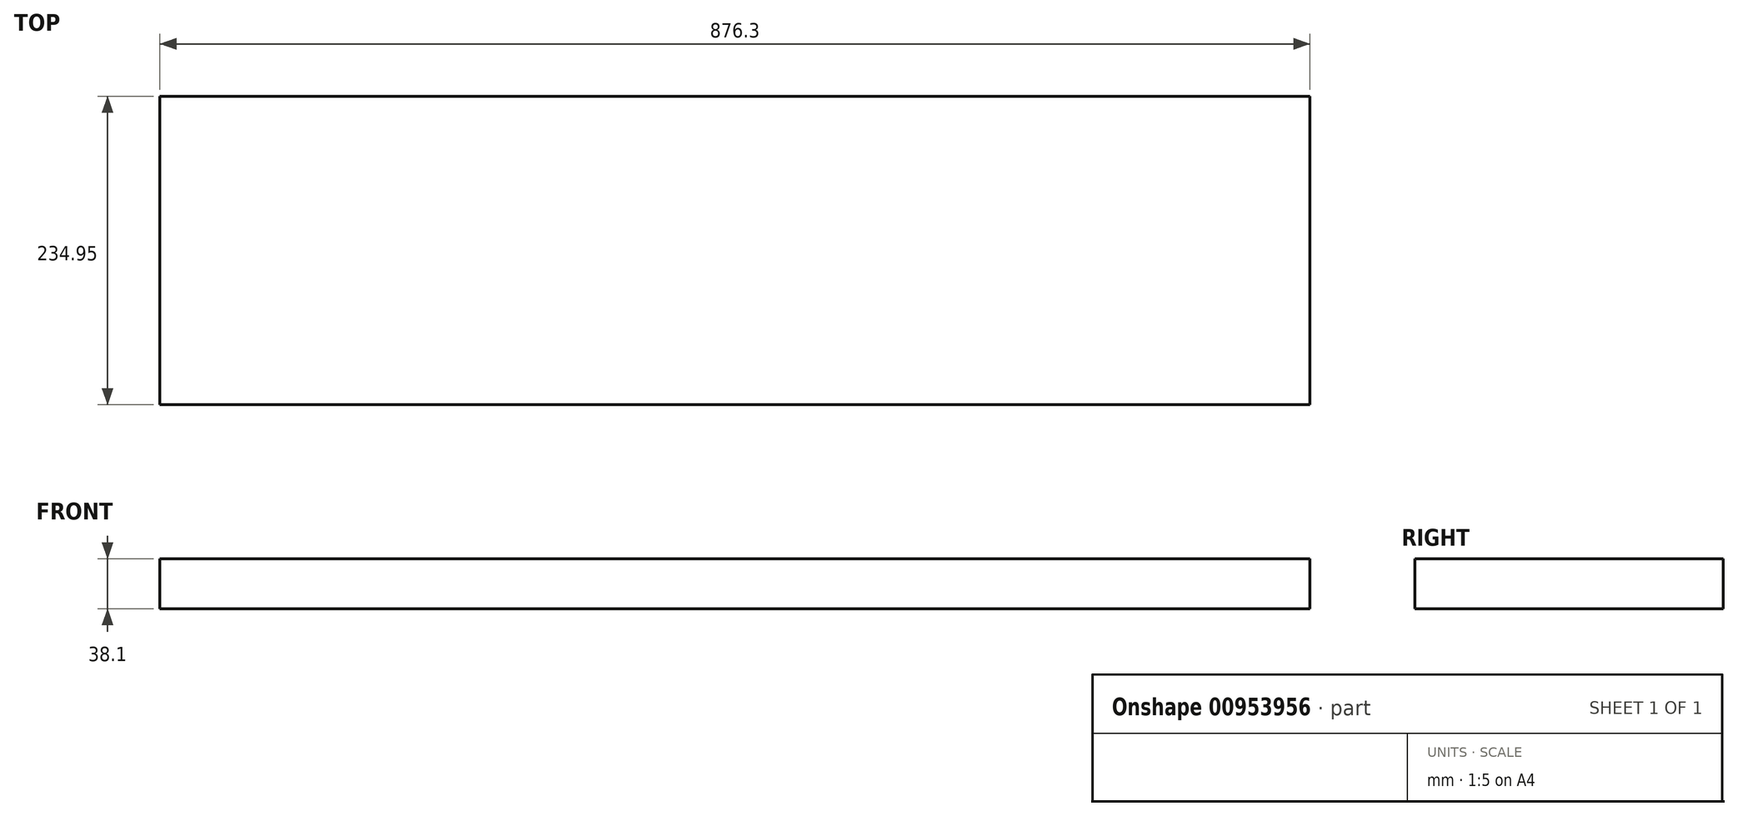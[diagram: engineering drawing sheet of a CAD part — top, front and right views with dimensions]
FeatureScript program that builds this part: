
annotation { "Feature Type Name" : "Feature", "Feature Type Description" : "" }
export const myFeature = defineFeature(function(context is Context, id is Id, definition is map)
    precondition{}
    {
        {
            var Q0;
            Q0=qCreatedBy(makeId("Top.planeOp"),FACE);
            var sketch = newSketch(context, id + "F0", { "sketchPlane" : qUnion([Q0])});
            skLineSegment(sketch, "E0.bottom", {"start": v(0, 0) * mm, "end": v(876.3, 0) * mm});
            skLineSegment(sketch, "E0.top", {"start": v(0, 234.95) * mm, "end": v(876.3, 234.95) * mm});
            skLineSegment(sketch, "E0.left", {"start": v(0, 0) * mm, "end": v(0, 234.95) * mm});
            skLineSegment(sketch, "E0.right", {"start": v(876.3, 0) * mm, "end": v(876.3, 234.95) * mm});
            skSolve(sketch);
        }
        {
            var Q0;
            Q0=qSketchRegion(id+"F0",true);
            extrude(context, id + "F1", {"entities" : qUnion([Q0]), "depth" : 38.1 * mm, "offsetDistance" : 25.4 * mm});
        }
    });
